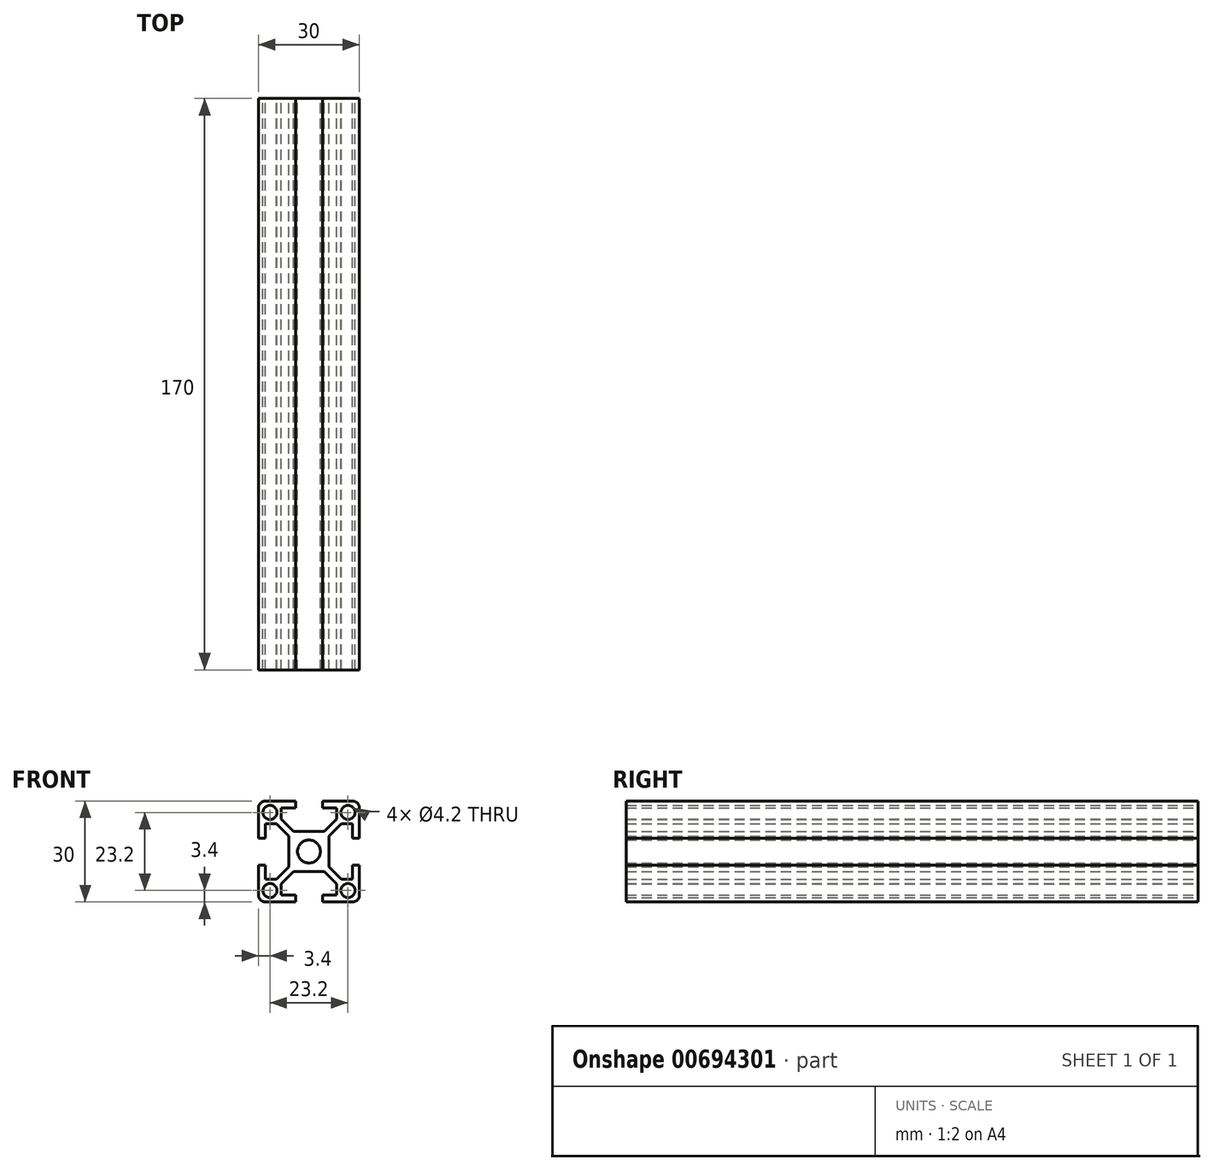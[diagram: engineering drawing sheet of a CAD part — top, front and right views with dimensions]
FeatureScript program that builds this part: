
annotation { "Feature Type Name" : "Feature", "Feature Type Description" : "" }
export const myFeature = defineFeature(function(context is Context, id is Id, definition is map)
    precondition{}
    {
        {
            var Q0;
            Q0=qCreatedBy(makeId("Front.planeOp"),FACE);
            var sketch = newSketch(context, id + "F0", { "sketchPlane" : qUnion([Q0])});
            skLineSegment(sketch, "E0", {"start": v(0, 6) * mm, "end": v(-4.59, 6) * mm});
            skLineSegment(sketch, "E1", {"start": v(-4.59, 6) * mm, "end": v(-8.25, 9.66) * mm});
            skLineSegment(sketch, "E2", {"start": v(-8.25, 9.66) * mm, "end": v(-8.25, 13) * mm});
            skLineSegment(sketch, "E3", {"start": v(-8.25, 13) * mm, "end": v(-4, 13) * mm});
            skLineSegment(sketch, "E4", {"start": v(-4, 13) * mm, "end": v(-4, 15) * mm});
            skLineSegment(sketch, "E5", {"start": v(-4, 15) * mm, "end": v(-13, 15) * mm});
            skLineSegment(sketch, "E6", {"start": v(-15, 13) * mm, "end": v(-15, 4) * mm});
            skLineSegment(sketch, "E7", {"start": v(-15, 4) * mm, "end": v(-13, 4) * mm});
            skLineSegment(sketch, "E8", {"start": v(-13, 4) * mm, "end": v(-13, 8.25) * mm});
            skLineSegment(sketch, "E9", {"start": v(-13, 8.25) * mm, "end": v(-9.66, 8.25) * mm});
            skLineSegment(sketch, "E10", {"start": v(-9.66, 8.25) * mm, "end": v(-6, 4.59) * mm});
            skLineSegment(sketch, "E11", {"start": v(-6, 4.59) * mm, "end": v(-6, 0) * mm});
            skLineSegment(sketch, "E12", {"start": v(-6, 0) * mm, "end": v(0, 0) * mm, "construction": true});
            skLineSegment(sketch, "E13", {"start": v(0, 0) * mm, "end": v(0, 6) * mm, "construction": true});
            skArc(sketch, "E14", {"start": v(0, 3.4) * mm, "mid": v(-2.4, 2.4) * mm, "end": v(-3.4, 0) * mm});
            skCircle(sketch, "E15", {"center": v(-11.6, 11.6) * mm, "radius": 2.1 * mm});
            skLineSegment(sketch, "E16", {"start": v(0, 0) * mm, "end": v(-7.38, 7.38) * mm, "construction": true});
            skLineSegment(sketch, "E17.1.0", {"start": v(-8.25, -13) * mm, "end": v(-8.25, -9.66) * mm});
            skLineSegment(sketch, "E17.1.1", {"start": v(-4, -15) * mm, "end": v(-4, -13) * mm});
            skLineSegment(sketch, "E17.1.2", {"start": v(-4, -13) * mm, "end": v(-8.25, -13) * mm});
            skLineSegment(sketch, "E17.1.3", {"start": v(-15, -4) * mm, "end": v(-15, -13) * mm});
            skLineSegment(sketch, "E17.1.4", {"start": v(-8.25, -9.66) * mm, "end": v(-4.59, -6) * mm});
            skLineSegment(sketch, "E17.1.5", {"start": v(-13, -15) * mm, "end": v(-4, -15) * mm});
            skLineSegment(sketch, "E17.1.6", {"start": v(-4.59, -6) * mm, "end": v(0, -6) * mm});
            skLineSegment(sketch, "E17.1.7", {"start": v(0, -6) * mm, "end": v(0, 0) * mm, "construction": true});
            skLineSegment(sketch, "E17.1.8", {"start": v(0, 0) * mm, "end": v(-6, 0) * mm, "construction": true});
            skLineSegment(sketch, "E17.1.9", {"start": v(-13, -4) * mm, "end": v(-15, -4) * mm});
            skLineSegment(sketch, "E17.1.10", {"start": v(-13, -8.25) * mm, "end": v(-13, -4) * mm});
            skArc(sketch, "E17.1.11", {"start": v(-3.4, 0) * mm, "mid": v(-2.4, -2.4) * mm, "end": v(0, -3.4) * mm});
            skLineSegment(sketch, "E17.1.12", {"start": v(-9.66, -8.25) * mm, "end": v(-13, -8.25) * mm});
            skLineSegment(sketch, "E17.1.13", {"start": v(0, 0) * mm, "end": v(-7.38, -7.38) * mm, "construction": true});
            skLineSegment(sketch, "E17.1.14", {"start": v(-6, -4.59) * mm, "end": v(-9.66, -8.25) * mm});
            skCircle(sketch, "E17.1.15", {"center": v(-11.6, -11.6) * mm, "radius": 2.1 * mm});
            skLineSegment(sketch, "E17.1.16", {"start": v(-6, 0) * mm, "end": v(-6, -4.59) * mm});
            skLineSegment(sketch, "E17.2.0", {"start": v(13, -8.25) * mm, "end": v(9.66, -8.25) * mm});
            skLineSegment(sketch, "E17.2.1", {"start": v(15, -4) * mm, "end": v(13, -4) * mm});
            skLineSegment(sketch, "E17.2.2", {"start": v(13, -4) * mm, "end": v(13, -8.25) * mm});
            skLineSegment(sketch, "E17.2.3", {"start": v(4, -15) * mm, "end": v(13, -15) * mm});
            skLineSegment(sketch, "E17.2.4", {"start": v(9.66, -8.25) * mm, "end": v(6, -4.59) * mm});
            skLineSegment(sketch, "E17.2.5", {"start": v(15, -13) * mm, "end": v(15, -4) * mm});
            skLineSegment(sketch, "E17.2.6", {"start": v(6, -4.59) * mm, "end": v(6, 0) * mm});
            skLineSegment(sketch, "E17.2.7", {"start": v(6, 0) * mm, "end": v(0, 0) * mm, "construction": true});
            skLineSegment(sketch, "E17.2.8", {"start": v(0, 0) * mm, "end": v(0, -6) * mm, "construction": true});
            skLineSegment(sketch, "E17.2.9", {"start": v(4, -13) * mm, "end": v(4, -15) * mm});
            skLineSegment(sketch, "E17.2.10", {"start": v(8.25, -13) * mm, "end": v(4, -13) * mm});
            skArc(sketch, "E17.2.11", {"start": v(0, -3.4) * mm, "mid": v(2.4, -2.4) * mm, "end": v(3.4, 0) * mm});
            skLineSegment(sketch, "E17.2.12", {"start": v(8.25, -9.66) * mm, "end": v(8.25, -13) * mm});
            skLineSegment(sketch, "E17.2.13", {"start": v(0, 0) * mm, "end": v(7.38, -7.38) * mm, "construction": true});
            skLineSegment(sketch, "E17.2.14", {"start": v(4.59, -6) * mm, "end": v(8.25, -9.66) * mm});
            skCircle(sketch, "E17.2.15", {"center": v(11.6, -11.6) * mm, "radius": 2.1 * mm});
            skLineSegment(sketch, "E17.2.16", {"start": v(0, -6) * mm, "end": v(4.59, -6) * mm});
            skLineSegment(sketch, "E17.3.0", {"start": v(8.25, 13) * mm, "end": v(8.25, 9.66) * mm});
            skLineSegment(sketch, "E17.3.1", {"start": v(4, 15) * mm, "end": v(4, 13) * mm});
            skLineSegment(sketch, "E17.3.2", {"start": v(4, 13) * mm, "end": v(8.25, 13) * mm});
            skLineSegment(sketch, "E17.3.3", {"start": v(15, 4) * mm, "end": v(15, 13) * mm});
            skLineSegment(sketch, "E17.3.4", {"start": v(8.25, 9.66) * mm, "end": v(4.59, 6) * mm});
            skLineSegment(sketch, "E17.3.5", {"start": v(13, 15) * mm, "end": v(4, 15) * mm});
            skLineSegment(sketch, "E17.3.6", {"start": v(4.59, 6) * mm, "end": v(0, 6) * mm});
            skLineSegment(sketch, "E17.3.7", {"start": v(0, 6) * mm, "end": v(0, 0) * mm, "construction": true});
            skLineSegment(sketch, "E17.3.8", {"start": v(0, 0) * mm, "end": v(6, 0) * mm, "construction": true});
            skLineSegment(sketch, "E17.3.9", {"start": v(13, 4) * mm, "end": v(15, 4) * mm});
            skLineSegment(sketch, "E17.3.10", {"start": v(13, 8.25) * mm, "end": v(13, 4) * mm});
            skArc(sketch, "E17.3.11", {"start": v(3.4, 0) * mm, "mid": v(2.4, 2.4) * mm, "end": v(0, 3.4) * mm});
            skLineSegment(sketch, "E17.3.12", {"start": v(9.66, 8.25) * mm, "end": v(13, 8.25) * mm});
            skLineSegment(sketch, "E17.3.13", {"start": v(0, 0) * mm, "end": v(7.38, 7.38) * mm, "construction": true});
            skLineSegment(sketch, "E17.3.14", {"start": v(6, 4.59) * mm, "end": v(9.66, 8.25) * mm});
            skCircle(sketch, "E17.3.15", {"center": v(11.6, 11.6) * mm, "radius": 2.1 * mm});
            skLineSegment(sketch, "E17.3.16", {"start": v(6, 0) * mm, "end": v(6, 4.59) * mm});
            skPoint(sketch, "E18.visualSharp", {"position": v(-15, 15) * mm});
            skArc(sketch, "E18.filletArc", {"start": v(-13, 15) * mm, "mid": v(-14.41, 14.41) * mm, "end": v(-15, 13) * mm});
            skPoint(sketch, "E19.visualSharp", {"position": v(15, 15) * mm});
            skArc(sketch, "E19.filletArc", {"start": v(15, 13) * mm, "mid": v(14.41, 14.41) * mm, "end": v(13, 15) * mm});
            skPoint(sketch, "E20.visualSharp", {"position": v(15, -15) * mm});
            skArc(sketch, "E20.filletArc", {"start": v(13, -15) * mm, "mid": v(14.41, -14.41) * mm, "end": v(15, -13) * mm});
            skPoint(sketch, "E21.visualSharp", {"position": v(-15, -15) * mm});
            skArc(sketch, "E21.filletArc", {"start": v(-15, -13) * mm, "mid": v(-14.41, -14.41) * mm, "end": v(-13, -15) * mm});
            skSolve(sketch);
        }
        {
            var Q0;
            Q0=qSketchRegion(id+"F0",true);
            extrude(context, id + "F1", {"entities" : qUnion([Q0]), "depth" : 170 * mm, "offsetDistance" : 25 * mm});
        }
    });
